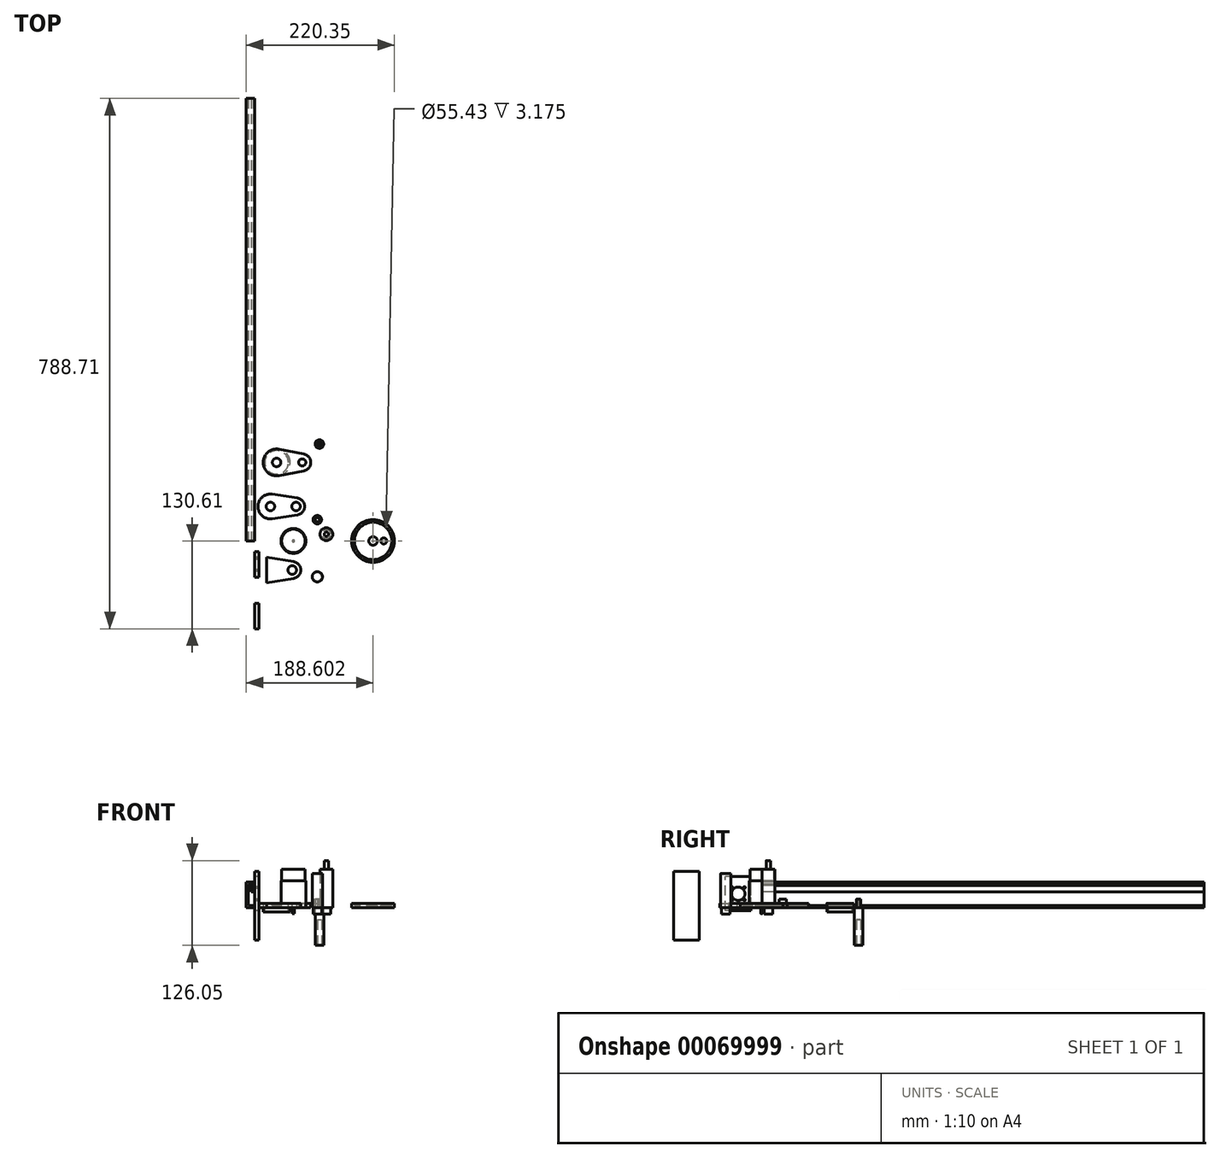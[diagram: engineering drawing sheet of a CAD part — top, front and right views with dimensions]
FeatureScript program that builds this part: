
annotation { "Feature Type Name" : "Feature", "Feature Type Description" : "" }
export const myFeature = defineFeature(function(context is Context, id is Id, definition is map)
    precondition{}
    {
        {
            var Q0;
            Q0=qCreatedBy(makeId("Front.planeOp"),FACE);
            var sketch = newSketch(context, id + "F0", { "sketchPlane" : qUnion([Q0])});
            skLineSegment(sketch, "E0.bottom", {"start": v(-12.57, 38.1) * mm, "end": v(0.13, 38.1) * mm});
            skLineSegment(sketch, "E0.top", {"start": v(-12.57, 0) * mm, "end": v(0, 0) * mm});
            skLineSegment(sketch, "E0.left", {"start": v(-12.57, 38.1) * mm, "end": v(-12.57, 0) * mm});
            skLineSegment(sketch, "E1", {"start": v(0.13, 3.17) * mm, "end": v(-9.4, 3.17) * mm});
            skLineSegment(sketch, "E2", {"start": v(-9.4, 3.17) * mm, "end": v(-9.4, 34.92) * mm});
            skLineSegment(sketch, "E3", {"start": v(-9.4, 34.92) * mm, "end": v(0, 34.92) * mm});
            skLineSegment(sketch, "E4", {"start": v(0, 0) * mm, "end": v(0.13, 3.17) * mm});
            skLineSegment(sketch, "E5", {"start": v(0.13, 38.1) * mm, "end": v(0, 34.92) * mm});
            skSolve(sketch);
        }
        {
            var Q0;
            Q0 = qSketchRegion(id + "F0", true);
            extrude(context, id + "F1", {"entities" : qUnion([Q0]), "oppositeDirection" : true, "depth" : 620 * mm + 38.1 * mm});
        }
        {
            var Q0;
            Q0=qCreatedBy(makeId("Front.planeOp"),FACE);
            var sketch = newSketch(context, id + "F2", { "sketchPlane" : qUnion([Q0])});
            skLineSegment(sketch, "E6.bottom", {"start": v(-4.96, 32.93) * mm, "end": v(-1.78, 32.93) * mm});
            skLineSegment(sketch, "E6.top", {"start": v(-4.96, 23) * mm, "end": v(-1.78, 23) * mm});
            skLineSegment(sketch, "E6.left", {"start": v(-4.96, 32.93) * mm, "end": v(-4.96, 23) * mm});
            skLineSegment(sketch, "E6.right", {"start": v(-1.78, 32.93) * mm, "end": v(-1.78, 23) * mm});
            skSolve(sketch);
        }
        {
            var Q0;
            Q0 = qSketchRegion(id + "F2", true);
            extrude(context, id + "F3", {"entities" : qUnion([Q0]), "oppositeDirection" : true, "depth" : 620 * mm + 38.1 * mm});
        }
        {
            var Q0;
            Q0=qCreatedBy(makeId("Right.planeOp"),FACE);
            var sketch = newSketch(context, id + "F4", { "sketchPlane" : qUnion([Q0])});
            skPoint(sketch, "E7.center", {"position": v(-34.78, 20.42) * mm});
            skCircle(sketch, "E8", {"center": v(-34.78, 20.42) * mm, "radius": 10 * mm});
            skCircle(sketch, "E9", {"center": v(-43.98, 29.63) * mm, "radius": 1.5 * mm});
            skCircle(sketch, "E7.1.0", {"center": v(-43.98, 11.22) * mm, "radius": 1.5 * mm});
            skCircle(sketch, "E7.2.0", {"center": v(-25.57, 11.22) * mm, "radius": 1.5 * mm});
            skCircle(sketch, "E7.3.0", {"center": v(-25.57, 29.63) * mm, "radius": 1.5 * mm});
            skCircle(sketch, "E10", {"center": v(-34.78, 20.42) * mm, "radius": 13 * mm, "construction": true});
            skLineSegment(sketch, "E11.bottom", {"start": v(-15.73, -4.98) * mm, "end": v(-53.83, -4.98) * mm});
            skLineSegment(sketch, "E11.top", {"start": v(-15.73, 45.82) * mm, "end": v(-53.83, 45.82) * mm});
            skLineSegment(sketch, "E11.left", {"start": v(-15.73, -4.98) * mm, "end": v(-15.73, 45.82) * mm});
            skLineSegment(sketch, "E11.right", {"start": v(-53.83, -4.98) * mm, "end": v(-53.83, 45.82) * mm});
            skSolve(sketch);
        }
        {
            var Q0;
            Q0 = qSketchRegion(id + "F4", true);
            extrude(context, id + "F5", {"entities" : qUnion([Q0]), "depth" : 6.35 * mm});
        }
        {
            var Q0;
            Q0=qCreatedBy(makeId("Top.planeOp"),FACE);
            var sketch = newSketch(context, id + "F6", { "sketchPlane" : qUnion([Q0])});
            skCircle(sketch, "E12", {"center": v(57.63, 0) * mm, "radius": 18.5 * mm});
            skSolve(sketch);
        }
        {
            var Q0;
            Q0=makeQuery(id+"F6.imprint","IMPRINT",FACE,{"disambiguationData":[TD([[makeQuery(id+"F6.imprint","IMPRINT",EDGE,{"derivedFrom":sQuery(id+"F6.wireOp",EDGE,"E12")}),1.0]])]});
            extrude(context, id + "F7", {"entities" : qUnion([Q0]), "depth" : 40 * mm});
        }
        {
            var Q0;
            Q0=makeQuery(id+"F7.opExtrude","CAP_FACE",FACE,{"disambiguationData":[OSD([sQuery(id+"F6.wireOp",EDGE,"E12")])],"isStart":false});
            var sketch = newSketch(context, id + "F8", { "sketchPlane" : qUnion([Q0])});
            skCircle(sketch, "E13", {"center": v(57.63, 0) * mm, "radius": 17.5 * mm});
            skSolve(sketch);
        }
        {
            var Q0;
            Q0 = qSketchRegion(id + "F8", true);
            extrude(context, id + "F9", {"entities" : qUnion([Q0]), "operationType" : NewBodyOperationType.ADD, "depth" : 17 * mm});
        }
        {
            var Q0;
            Q0=makeQuery(id+"F7.opExtrude","CAP_FACE",FACE,{"disambiguationData":[OSD([sQuery(id+"F6.wireOp",EDGE,"E12")])],"isStart":true});
            var sketch = newSketch(context, id + "F10", { "sketchPlane" : qUnion([Q0])});
            skCircle(sketch, "E14", {"center": v(57.63, 0) * mm, "radius": 1.5 * mm});
            skSolve(sketch);
        }
        {
            var Q0;
            Q0 = qSketchRegion(id + "F10", true);
            extrude(context, id + "F11", {"entities" : qUnion([Q0]), "operationType" : NewBodyOperationType.ADD, "depth" : 9 * mm});
        }
        {
            var Q0;
            Q0=qCreatedBy(makeId("Top.planeOp"),FACE);
            var sketch = newSketch(context, id + "F12", { "sketchPlane" : qUnion([Q0])});
            skLineSegment(sketch, "E15", {"start": v(17.75, -24.22) * mm, "end": v(17.75, -62.32) * mm});
            skPoint(sketch, "E16.visualSharp", {"position": v(96.49, -43.27) * mm});
            skLineSegment(sketch, "E17", {"start": v(17.75, -43.27) * mm, "end": v(107.02, -43.27) * mm, "construction": true});
            skCircle(sketch, "E18", {"center": v(55.85, -43.27) * mm, "radius": 6.35 * mm});
            skCircle(sketch, "E19", {"center": v(55.85, -43.27) * mm, "radius": 18.5 * mm, "construction": true});
            skArc(sketch, "E20", {"start": v(57.88, -55.8) * mm, "mid": v(68.55, -43.27) * mm, "end": v(57.88, -30.73) * mm});
            skLineSegment(sketch, "E21", {"start": v(17.75, -62.32) * mm, "end": v(57.88, -55.8) * mm});
            skLineSegment(sketch, "E22", {"start": v(17.75, -24.22) * mm, "end": v(57.88, -30.73) * mm});
            skSolve(sketch);
        }
        {
            var Q0;
            Q0=makeQuery(id+"F12.imprint","IMPRINT",FACE,{"disambiguationData":[TD([[makeQuery(id+"F12.imprint","IMPRINT",EDGE,{"derivedFrom":sQuery(id+"F12.wireOp",EDGE,"E15")}),1.0]])]});
            extrude(context, id + "F13", {"entities" : qUnion([Q0]), "depth" : 6.35 * mm});
        }
        {
            var Q0;
            Q0=qCreatedBy(makeId("Top.planeOp"),FACE);
            var sketch = newSketch(context, id + "F14", { "sketchPlane" : qUnion([Q0])});
            skArc(sketch, "E23", {"start": v(26.2, 69.56) * mm, "mid": v(4.88, 51.27) * mm, "end": v(26.2, 32.99) * mm});
            skArc(sketch, "E24", {"start": v(63.42, 38.72) * mm, "mid": v(74.18, 51.27) * mm, "end": v(63.42, 63.82) * mm});
            skLineSegment(sketch, "E25", {"start": v(26.2, 32.99) * mm, "end": v(63.42, 38.72) * mm});
            skLineSegment(sketch, "E26", {"start": v(26.2, 69.56) * mm, "end": v(63.42, 63.82) * mm});
            skCircle(sketch, "E27", {"center": v(61.48, 51.27) * mm, "radius": 6.35 * mm});
            skCircle(sketch, "E28", {"center": v(23.38, 51.27) * mm, "radius": 6.35 * mm});
            skSolve(sketch);
        }
        {
            var Q0;
            Q0 = qSketchRegion(id + "F14", true);
            extrude(context, id + "F15", {"entities" : qUnion([Q0]), "depth" : 6.35 * mm});
        }
        {
            var Q0;
            Q0=qCreatedBy(makeId("Top.planeOp"),FACE);
            var sketch = newSketch(context, id + "F16", { "sketchPlane" : qUnion([Q0])});
            skArc(sketch, "E29", {"start": v(36.45, 136.44) * mm, "mid": v(12.62, 116.81) * mm, "end": v(36.45, 97.18) * mm});
            skCircle(sketch, "E30", {"center": v(70.72, 116.81) * mm, "radius": 5.32 * mm});
            skArc(sketch, "E31", {"start": v(73.16, 104.35) * mm, "mid": v(83.42, 116.81) * mm, "end": v(73.16, 129.28) * mm});
            skLineSegment(sketch, "E32", {"start": v(36.45, 136.44) * mm, "end": v(73.16, 129.28) * mm});
            skLineSegment(sketch, "E33", {"start": v(73.16, 104.35) * mm, "end": v(36.45, 97.18) * mm});
            skSolve(sketch);
        }
        {
            var Q0;
            Q0=qCreatedBy(makeId("Top.planeOp"),FACE);
            var sketch = newSketch(context, id + "F17", { "sketchPlane" : qUnion([Q0])});
            skCircle(sketch, "E34", {"center": v(96.23, 144.14) * mm, "radius": 3.18 * mm});
            skSolve(sketch);
        }
        {
            var Q0;
            Q0 = qSketchRegion(id + "F17", true);
            extrude(context, id + "F18", {"entities" : qUnion([Q0]), "depth" : 12.7 * mm});
        }
        {
            var Q0;
            Q0=makeQuery(id+"F18.opExtrude","CAP_FACE",FACE,{"disambiguationData":[OSD([sQuery(id+"F17.wireOp",EDGE,"E34")])],"isStart":true});
            var sketch = newSketch(context, id + "F19", { "sketchPlane" : qUnion([Q0])});
            skCircle(sketch, "E35", {"center": v(96.23, -144.14) * mm, "radius": 6.35 * mm});
            skSolve(sketch);
        }
        {
            var Q0;
            Q0 = qSketchRegion(id + "F19", true);
            extrude(context, id + "F20", {"entities" : qUnion([Q0]), "operationType" : NewBodyOperationType.ADD, "depth" : 50 * mm + 6.35 * mm});
        }
        {
            var Q0;
            Q0=makeQuery(id+"F18.opExtrude","CAP_FACE",FACE,{"disambiguationData":[OSD([sQuery(id+"F17.wireOp",EDGE,"E34")])],"isStart":false});
            var sketch = newSketch(context, id + "F21", { "sketchPlane" : qUnion([Q0])});
            skCircle(sketch, "E36", {"center": v(96.23, 144.14) * mm, "radius": 1.5 * mm});
            skSolve(sketch);
        }
        {
            var Q0;
            Q0 = qSketchRegion(id + "F21", true);
            extrude(context, id + "F22", {"entities" : qUnion([Q0]), "operationType" : NewBodyOperationType.REMOVE, "oppositeDirection" : true, "depth" : 9 * mm});
        }
        {
            var Q0;
            Q0=makeQuery(id+"F20.opExtrude","CAP_FACE",FACE,{"disambiguationData":[OSD([sQuery(id+"F19.wireOp",EDGE,"E35")])],"isStart":false});
            var sketch = newSketch(context, id + "F23", { "sketchPlane" : qUnion([Q0])});
            skCircle(sketch, "E37", {"center": v(96.23, -144.14) * mm, "radius": 3.18 * mm});
            skSolve(sketch);
        }
        {
            var Q0;
            Q0=makeQuery(id+"F23.imprint","IMPRINT",FACE,{"disambiguationData":[TD([[makeQuery(id+"F23.imprint","IMPRINT",EDGE,{"derivedFrom":sQuery(id+"F23.wireOp",EDGE,"E37")}),1.0]])]});
            extrude(context, id + "F24", {"entities" : qUnion([Q0]), "operationType" : NewBodyOperationType.REMOVE, "oppositeDirection" : true, "depth" : 38.1 * mm});
        }
        {
            var Q0;
            Q0=qCreatedBy(makeId("Top.planeOp"),FACE);
            var sketch = newSketch(context, id + "F25", { "sketchPlane" : qUnion([Q0])});
            skCircle(sketch, "E38", {"center": v(93.1, 31.63) * mm, "radius": 5.32 * mm});
            skCircle(sketch, "E39", {"center": v(93.1, 31.63) * mm, "radius": 3.18 * mm});
            skSolve(sketch);
        }
        {
            var Q0;
            Q0=makeQuery(id+"F25.imprint","IMPRINT",FACE,{"disambiguationData":[TD([[makeQuery(id+"F25.imprint","IMPRINT",EDGE,{"derivedFrom":sQuery(id+"F25.wireOp",EDGE,"E38")}),1.0]])]});
            extrude(context, id + "F26", {"entities" : qUnion([Q0]), "depth" : 12.7 * mm});
        }
        {
            var Q0;
            Q0=makeQuery(id+"F16.imprint","IMPRINT",FACE,{"disambiguationData":[TD([[makeQuery(id+"F16.imprint","IMPRINT",EDGE,{"derivedFrom":sQuery(id+"F16.wireOp",EDGE,"E29")}),1.0]])]});
            extrude(context, id + "F27", {"entities" : qUnion([Q0]), "depth" : 6.35 * mm});
        }
        {
            var Q0;
            Q0=makeQuery(id+"F27.opExtrude","CAP_FACE",FACE,{"disambiguationData":[OSD([sQuery(id+"F16.wireOp",EDGE,"E29"),sQuery(id+"F16.wireOp",EDGE,"E30"),sQuery(id+"F16.wireOp",EDGE,"E31"),sQuery(id+"F16.wireOp",EDGE,"E32"),sQuery(id+"F16.wireOp",EDGE,"E33")])],"isStart":false});
            var sketch = newSketch(context, id + "F28", { "sketchPlane" : qUnion([Q0])});
            skCircle(sketch, "E40", {"center": v(32.62, 116.81) * mm, "radius": 6.35 * mm});
            skSolve(sketch);
        }
        {
            var Q0;
            Q0=makeQuery(id+"F28.imprint","IMPRINT",FACE,{"disambiguationData":[TD([[makeQuery(id+"F28.imprint","IMPRINT",EDGE,{"derivedFrom":sQuery(id+"F28.wireOp",EDGE,"E40")}),1.0]])]});
            extrude(context, id + "F29", {"entities" : qUnion([Q0]), "operationType" : NewBodyOperationType.REMOVE, "oppositeDirection" : true, "depth" : 3.17 * mm});
        }
        {
            var Q0;
            Q0=makeQuery(id+"F27.opExtrude","CAP_FACE",FACE,{"disambiguationData":[OSD([sQuery(id+"F16.wireOp",EDGE,"E29"),sQuery(id+"F16.wireOp",EDGE,"E30"),sQuery(id+"F16.wireOp",EDGE,"E31"),sQuery(id+"F16.wireOp",EDGE,"E32"),sQuery(id+"F16.wireOp",EDGE,"E33")])],"isStart":true});
            var sketch = newSketch(context, id + "F30", { "sketchPlane" : qUnion([Q0])});
            skCircle(sketch, "E41", {"center": v(32.62, -116.81) * mm, "radius": 20 * mm});
            skCircle(sketch, "E42", {"center": v(32.62, -116.81) * mm, "radius": 17.5 * mm});
            skSolve(sketch);
        }
        {
            var Q0;
            {var subQ0=sQuery(id+"F30.wireOp",EDGE,"E41");Q0=makeQuery(id+"F30.imprint","IMPRINT",FACE,{"disambiguationData":[TD([[makeQuery(id+"F30.imprint","IMPRINT",EDGE,{"disambiguationData":[OD(0.0)],"derivedFrom":subQ0}),-1.0]])]});}
            extrude(context, id + "F31", {"entities" : qUnion([Q0]), "operationType" : NewBodyOperationType.ADD, "depth" : 6.35 * mm});
        }
        {
            var Q0;
            Q0=qCreatedBy(makeId("Top.planeOp"),FACE);
            var sketch = newSketch(context, id + "F32", { "sketchPlane" : qUnion([Q0])});
            skCircle(sketch, "E43", {"center": v(176.03, 0) * mm, "radius": 31.75 * mm});
            skCircle(sketch, "E44", {"center": v(176.03, 0) * mm, "radius": 6.35 * mm});
            skSolve(sketch);
        }
        {
            var Q0;
            Q0 = qSketchRegion(id + "F32", true);
            extrude(context, id + "F33", {"entities" : qUnion([Q0]), "depth" : 6.35 * mm});
        }
        {
            var Q0;
            Q0=makeQuery(id+"F33.opExtrude","CAP_FACE",FACE,{"disambiguationData":[OSD([sQuery(id+"F32.wireOp",EDGE,"E43"),sQuery(id+"F32.wireOp",EDGE,"E44")])],"isStart":false});
            var sketch = newSketch(context, id + "F34", { "sketchPlane" : qUnion([Q0])});
            skCircle(sketch, "E45", {"center": v(176.03, 0) * mm, "radius": 27.71 * mm});
            skSolve(sketch);
        }
        {
            var Q0;
            Q0=makeQuery(id+"F34.imprint","IMPRINT",FACE,{"disambiguationData":[TD([[makeQuery(id+"F34.imprint","IMPRINT",EDGE,{"derivedFrom":makeQuery(id+"F33.opExtrude","CAP_EDGE",EDGE,{"disambiguationData":[OSD([sQuery(id+"F32.wireOp",EDGE,"E44")])],"isStart":false})}),1.0]])]});
            var Q1;
            Q1=makeQuery(id+"F34.imprint","IMPRINT",FACE,{"disambiguationData":[TD([[makeQuery(id+"F34.imprint","IMPRINT",EDGE,{"derivedFrom":sQuery(id+"F34.wireOp",EDGE,"E45")}),1.0]])]});
            extrude(context, id + "F35", {"entities" : qUnion([Q0, Q1]), "operationType" : NewBodyOperationType.REMOVE, "oppositeDirection" : true, "depth" : 3.17 * mm});
        }
        {
            var Q0;
            Q0=qCreatedBy(makeId("Top.planeOp"),FACE);
            var sketch = newSketch(context, id + "F36", { "sketchPlane" : qUnion([Q0])});
            skCircle(sketch, "E46", {"center": v(106.62, 10.04) * mm, "radius": 9.53 * mm});
            skSolve(sketch);
        }
        {
            var Q0;
            Q0=makeQuery(id+"F36.imprint","IMPRINT",FACE,{"disambiguationData":[TD([[makeQuery(id+"F36.imprint","IMPRINT",EDGE,{"derivedFrom":sQuery(id+"F36.wireOp",EDGE,"E46")}),1.0]])]});
            extrude(context, id + "F37", {"entities" : qUnion([Q0]), "depth" : 57 * mm});
        }
        {
            var Q0;
            Q0=makeQuery(id+"F37.opExtrude","CAP_FACE",FACE,{"disambiguationData":[OSD([sQuery(id+"F36.wireOp",EDGE,"E46")])],"isStart":false});
            var sketch = newSketch(context, id + "F38", { "sketchPlane" : qUnion([Q0])});
            skCircle(sketch, "E47", {"center": v(106.62, 10.04) * mm, "radius": 3.18 * mm});
            skSolve(sketch);
        }
        {
            var Q0;
            Q0 = qSketchRegion(id + "F38", true);
            extrude(context, id + "F39", {"entities" : qUnion([Q0]), "operationType" : NewBodyOperationType.ADD, "depth" : 12.7 * mm});
        }
        {
            var Q0;
            Q0=makeQuery(id+"F37.opExtrude","CAP_FACE",FACE,{"disambiguationData":[OSD([sQuery(id+"F36.wireOp",EDGE,"E46")])],"isStart":true});
            var sketch = newSketch(context, id + "F40", { "sketchPlane" : qUnion([Q0])});
            skCircle(sketch, "E48", {"center": v(106.62, -10.04) * mm, "radius": 6.35 * mm});
            skSolve(sketch);
        }
        {
            var Q0;
            Q0 = qSketchRegion(id + "F40", true);
            extrude(context, id + "F41", {"entities" : qUnion([Q0]), "operationType" : NewBodyOperationType.ADD, "depth" : 3.17 * mm + 6.35 * mm});
        }
        {
            var Q0;
            Q0=makeQuery(id+"F26.opExtrude","CAP_FACE",FACE,{"disambiguationData":[OSD([sQuery(id+"F25.wireOp",EDGE,"E38"),sQuery(id+"F25.wireOp",EDGE,"E39")])],"isStart":true});
            var sketch = newSketch(context, id + "F42", { "sketchPlane" : qUnion([Q0])});
            skCircle(sketch, "E49", {"center": v(93.1, -31.63) * mm, "radius": 6.35 * mm});
            skCircle(sketch, "E50", {"center": v(93.1, -31.63) * mm, "radius": 3.18 * mm});
            skSolve(sketch);
        }
        {
            var Q0;
            Q0=makeQuery(id+"F42.imprint","IMPRINT",FACE,{"disambiguationData":[TD([[makeQuery(id+"F42.imprint","IMPRINT",EDGE,{"derivedFrom":makeQuery(id+"F26.opExtrude","CAP_EDGE",EDGE,{"disambiguationData":[OSD([sQuery(id+"F25.wireOp",EDGE,"E39")])],"isStart":true})}),-1.0]])]});
            var Q1;
            Q1=makeQuery(id+"F42.imprint","IMPRINT",FACE,{"disambiguationData":[TD([[makeQuery(id+"F42.imprint","IMPRINT",EDGE,{"derivedFrom":makeQuery(id+"F26.opExtrude","CAP_EDGE",EDGE,{"disambiguationData":[OSD([sQuery(id+"F25.wireOp",EDGE,"E38")])],"isStart":true})}),-1.0]])]});
            var Q2;
            Q2=makeQuery(id+"F42.imprint","IMPRINT",FACE,{"disambiguationData":[TD([[makeQuery(id+"F42.imprint","IMPRINT",EDGE,{"derivedFrom":sQuery(id+"F42.wireOp",EDGE,"E49")}),1.0]])]});
            extrude(context, id + "F43", {"entities" : qUnion([Q0, Q1, Q2]), "operationType" : NewBodyOperationType.ADD, "oppositeDirection" : true, "depth" : 6.35 * mm});
        }
        {
            var Q0;
            Q0=qCreatedBy(makeId("Top.planeOp"),FACE);
            var sketch = newSketch(context, id + "F44", { "sketchPlane" : qUnion([Q0])});
            skCircle(sketch, "E51", {"center": v(93.2, -53.36) * mm, "radius": 7.62 * mm});
            skSolve(sketch);
        }
        {
            var Q0;
            Q0=makeQuery(id+"F44.imprint","IMPRINT",FACE,{"disambiguationData":[TD([[makeQuery(id+"F44.imprint","IMPRINT",EDGE,{"derivedFrom":sQuery(id+"F44.wireOp",EDGE,"E51")}),1.0]])]});
            extrude(context, id + "F45", {"entities" : qUnion([Q0]), "depth" : 50.8 * mm});
        }
        {
            var Q0;
            Q0=makeQuery(id+"F45.opExtrude","CAP_FACE",FACE,{"disambiguationData":[OSD([sQuery(id+"F44.wireOp",EDGE,"E51")])],"isStart":true});
            var sketch = newSketch(context, id + "F46", { "sketchPlane" : qUnion([Q0])});
            skCircle(sketch, "E52", {"center": v(93.2, 53.36) * mm, "radius": 6.35 * mm});
            skSolve(sketch);
        }
        {
            var Q0;
            Q0=makeQuery(id+"F46.imprint","IMPRINT",FACE,{"disambiguationData":[TD([[makeQuery(id+"F46.imprint","IMPRINT",EDGE,{"derivedFrom":sQuery(id+"F46.wireOp",EDGE,"E52")}),1.0]])]});
            extrude(context, id + "F47", {"entities" : qUnion([Q0]), "operationType" : NewBodyOperationType.ADD, "depth" : 9.52 * mm});
        }
        {
            var Q0;
            Q0=makeQuery(id+"F35.boolean.opBoolean","COPY",FACE,{"derivedFrom":makeQuery(id+"F35.opExtrude","CAP_FACE",FACE,{"disambiguationData":[OSD([sQuery(id+"F34.wireOp",EDGE,"E45")])],"isStart":false})});
            var sketch = newSketch(context, id + "F48", { "sketchPlane" : qUnion([Q0])});
            skCircle(sketch, "E53", {"center": v(191.9, 0) * mm, "radius": 4.45 * mm});
            skSolve(sketch);
        }
        {
            var Q0;
            Q0=makeQuery(id+"F48.imprint","IMPRINT",FACE,{"disambiguationData":[TD([[makeQuery(id+"F48.imprint","IMPRINT",EDGE,{"derivedFrom":sQuery(id+"F48.wireOp",EDGE,"E53")}),1.0]])]});
            extrude(context, id + "F49", {"entities" : qUnion([Q0]), "operationType" : NewBodyOperationType.REMOVE, "oppositeDirection" : true, "depth" : 3.17 * mm});
        }
        {
            var Q0;
            Q0=makeQuery(id+"F43.boolean.opBoolean","MERGE",FACE,{"derivedFrom":[makeQuery(id+"F26.opExtrude","CAP_FACE",FACE,{"disambiguationData":[OSD([sQuery(id+"F25.wireOp",EDGE,"E38"),sQuery(id+"F25.wireOp",EDGE,"E39")])],"isStart":true}),makeQuery(id+"F43.opExtrude","CAP_FACE",FACE,{"disambiguationData":[OSD([sQuery(id+"F42.wireOp",EDGE,"E49"),sQuery(id+"F42.wireOp",EDGE,"E50")])],"isStart":true})]});
            var sketch = newSketch(context, id + "F50", { "sketchPlane" : qUnion([Q0])});
            skCircle(sketch, "E54", {"center": v(97.67, -31.62) * mm, "radius": 0.64 * mm});
            skCircle(sketch, "E55", {"center": v(88.52, -31.62) * mm, "radius": 0.64 * mm});
            skSolve(sketch);
        }
        {
            var Q0;
            Q0=makeQuery(id+"F50.imprint","IMPRINT",FACE,{"disambiguationData":[TD([[makeQuery(id+"F50.imprint","IMPRINT",EDGE,{"derivedFrom":sQuery(id+"F50.wireOp",EDGE,"E55")}),1.0]])]});
            var Q1;
            Q1=makeQuery(id+"F50.imprint","IMPRINT",FACE,{"disambiguationData":[TD([[makeQuery(id+"F50.imprint","IMPRINT",EDGE,{"derivedFrom":sQuery(id+"F50.wireOp",EDGE,"E54")}),1.0]])]});
            extrude(context, id + "F51", {"entities" : qUnion([Q0, Q1]), "operationType" : NewBodyOperationType.REMOVE, "oppositeDirection" : true, "depth" : 3.17 * mm});
        }
        {
            var Q0;
            Q0=qCreatedBy(makeId("Right.planeOp"),FACE);
            var sketch = newSketch(context, id + "F52", { "sketchPlane" : qUnion([Q0])});
            skLineSegment(sketch, "E56.bottom", {"start": v(-92.51, 53.8) * mm, "end": v(-130.61, 53.8) * mm});
            skLineSegment(sketch, "E56.top", {"start": v(-92.51, -48.6) * mm, "end": v(-130.61, -48.6) * mm});
            skLineSegment(sketch, "E56.left", {"start": v(-92.51, 53.8) * mm, "end": v(-92.51, -48.6) * mm});
            skLineSegment(sketch, "E56.right", {"start": v(-130.61, 53.8) * mm, "end": v(-130.61, -48.6) * mm});
            skSolve(sketch);
        }
        {
            var Q0;
            Q0 = qSketchRegion(id + "F52", true);
            var Q1;
            Q1=makeQuery(id+"F52.imprint","IMPRINT",FACE,{"disambiguationData":[TD([[makeQuery(id+"F52.imprint","IMPRINT",EDGE,{"derivedFrom":sQuery(id+"F52.wireOp",EDGE,"E56.bottom")}),1.0]])]});
            extrude(context, id + "F53", {"entities" : qUnion([Q0, Q1]), "depth" : 6.35 * mm});
        }
    });
